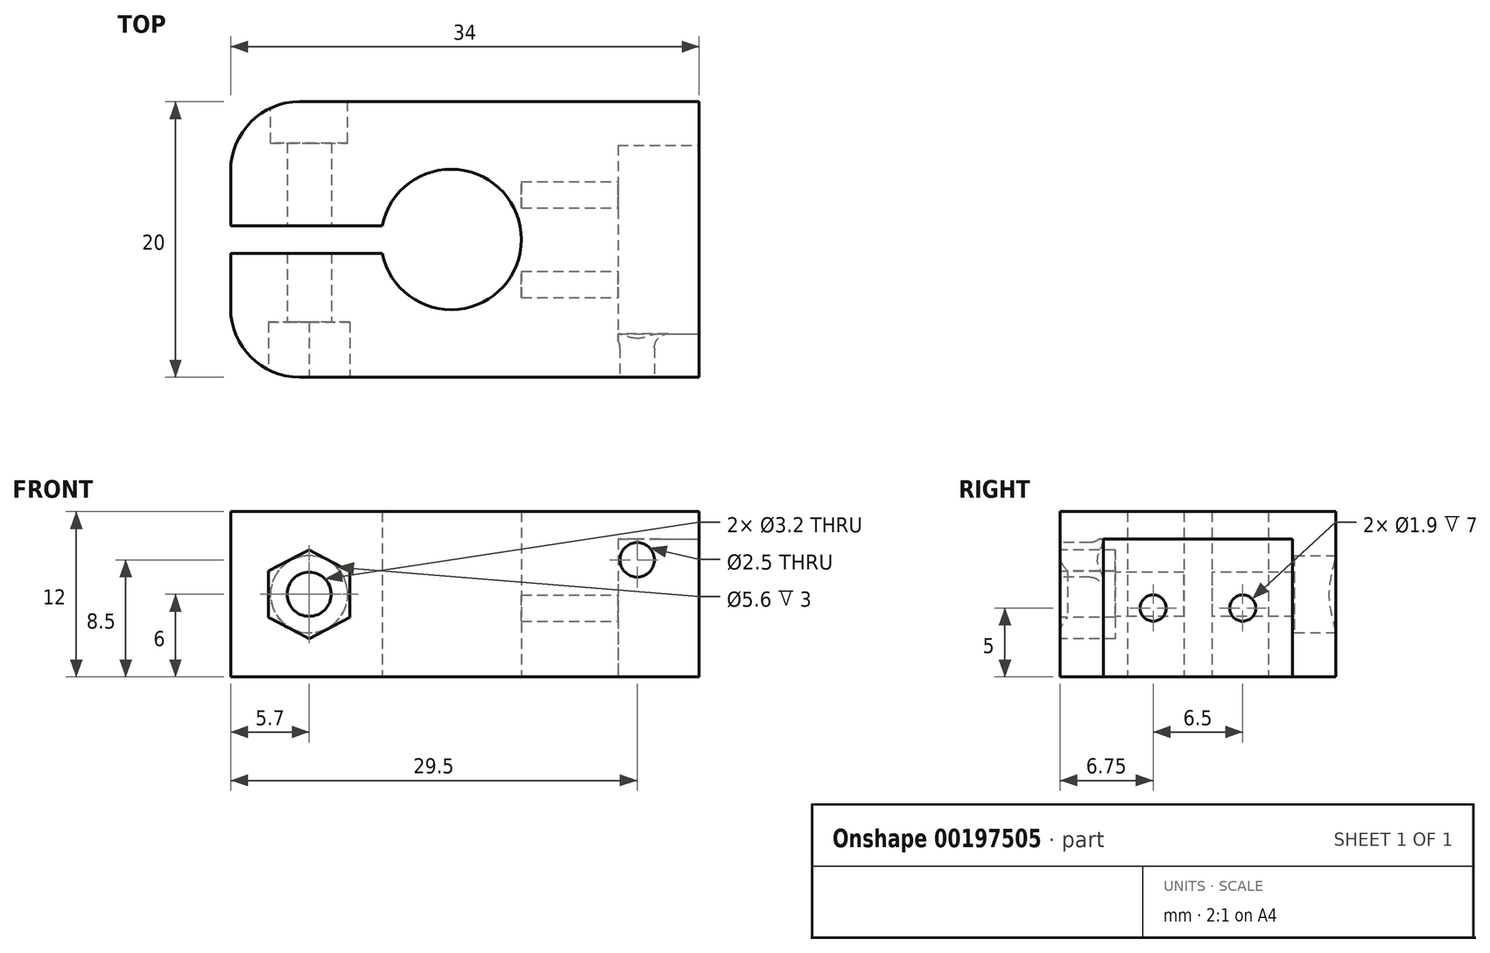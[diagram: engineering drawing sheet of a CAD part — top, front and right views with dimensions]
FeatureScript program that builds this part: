
annotation { "Feature Type Name" : "Feature", "Feature Type Description" : "" }
export const myFeature = defineFeature(function(context is Context, id is Id, definition is map)
    precondition{}
    {
        {
            var Q0;
            Q0=qCreatedBy(makeId("Top.planeOp"),FACE);
            var sketch = newSketch(context, id + "F0", { "sketchPlane" : qUnion([Q0])});
            skLineSegment(sketch, "E0.bottom", {"start": v(-16, 10) * mm, "end": v(18, 10) * mm});
            skLineSegment(sketch, "E0.top", {"start": v(-16, -10) * mm, "end": v(18, -10) * mm});
            skLineSegment(sketch, "E0.left", {"start": v(-16, 10) * mm, "end": v(-16, 1) * mm});
            skLineSegment(sketch, "E0.right", {"start": v(18, 10) * mm, "end": v(18, -10) * mm});
            skArc(sketch, "E1", {"start": v(-5, -1) * mm, "mid": v(5.1, 0) * mm, "end": v(-5, 1) * mm});
            skLineSegment(sketch, "E2.bottom", {"start": v(-16, 0) * mm, "end": v(-4.9, 0) * mm});
            skLineSegment(sketch, "E2.top", {"start": v(-16, 1) * mm, "end": v(-5, 1) * mm});
            skLineSegment(sketch, "E3.MirrorCS", {"start": v(-16, -1) * mm, "end": v(-5, -1) * mm});
            skPoint(sketch, "E4.MirrorCS.end.orphan", {"position": v(-5, -1) * mm});
            skPoint(sketch, "E4.MirrorCS.start.orphan", {"position": v(-4.9, 0) * mm});
            skPoint(sketch, "E5.MirrorCS.end.orphan", {"position": v(-16, -1) * mm});
            skPoint(sketch, "E5.MirrorCS.start.orphan", {"position": v(-16, 0) * mm});
            skLineSegment(sketch, "E6.trimOffspring", {"start": v(-16, -1) * mm, "end": v(-16, -10) * mm});
            skLineSegment(sketch, "E7.bottom", {"start": v(12.1, 6.85) * mm, "end": v(18, 6.85) * mm, "construction": true});
            skLineSegment(sketch, "E7.top", {"start": v(12.1, -6.85) * mm, "end": v(18, -6.85) * mm, "construction": true});
            skLineSegment(sketch, "E7.left", {"start": v(12.1, 6.85) * mm, "end": v(12.1, -6.85) * mm, "construction": true});
            skLineSegment(sketch, "E8.bottom", {"start": v(18, 6.85) * mm, "end": v(18, 6.85) * mm});
            skLineSegment(sketch, "E8.top", {"start": v(14.5, -6.85) * mm, "end": v(18, -6.85) * mm, "construction": true});
            skLineSegment(sketch, "E8.right", {"start": v(18, 6.85) * mm, "end": v(18, -6.85) * mm});
            skLineSegment(sketch, "E9", {"start": v(18, 6.85) * mm, "end": v(18, -6.85) * mm, "construction": true});
            skSolve(sketch);
        }
        {
            var Q0;
            Q0=qSketchRegion(id+"F0",true);
            extrude(context, id + "F1", {"entities" : qUnion([Q0]), "depth" : 12 * mm});
        }
        {
            var Q0;
            Q0=makeQuery(id+"F1.opExtrude","CAP_FACE",FACE,{"disambiguationData":[OSD([sQuery(id+"F0.wireOp",EDGE,"E0.bottom"),sQuery(id+"F0.wireOp",EDGE,"E0.top"),sQuery(id+"F0.wireOp",EDGE,"E0.left"),sQuery(id+"F0.wireOp",EDGE,"E0.right"),sQuery(id+"F0.wireOp",EDGE,"E1"),sQuery(id+"F0.wireOp",EDGE,"E2.top"),sQuery(id+"F0.wireOp",EDGE,"E3.MirrorCS"),sQuery(id+"F0.wireOp",EDGE,"E6.trimOffspring"),sQuery(id+"F0.wireOp",EDGE,"E8.right")])],"isStart":true});
            var sketch = newSketch(context, id + "F2", { "sketchPlane" : qUnion([Q0])});
            skLineSegment(sketch, "E10.0", {"start": v(12.1, -6.85) * mm, "end": v(12.1, 6.85) * mm});
            skLineSegment(sketch, "E11.0", {"start": v(12.1, 6.85) * mm, "end": v(18, 6.85) * mm});
            skLineSegment(sketch, "E12.0", {"start": v(18, 6.85) * mm, "end": v(18, 6.85) * mm});
            skLineSegment(sketch, "E13.0", {"start": v(12.1, -6.85) * mm, "end": v(18, -6.85) * mm});
            skLineSegment(sketch, "E14", {"start": v(18, 6.85) * mm, "end": v(18, -6.85) * mm});
            skSolve(sketch);
        }
        {
            var Q0;
            Q0=qSketchRegion(id+"F2",true);
            extrude(context, id + "F3", {"entities" : qUnion([Q0]), "operationType" : NewBodyOperationType.REMOVE, "oppositeDirection" : true, "depth" : 10 * mm});
        }
        {
            var Q0;
            Q0=makeQuery(id+"F1.opExtrude","SWEPT_FACE",FACE,{"disambiguationData":[OSD([sQuery(id+"F0.wireOp",EDGE,"E0.top")])]});
            var sketch = newSketch(context, id + "F4", { "sketchPlane" : qUnion([Q0])});
            skCircle(sketch, "E15", {"center": v(-10.3, 6) * mm, "radius": 1.6 * mm});
            skPoint(sketch, "E15.centerSnap0", {"position": v(-16, 6) * mm});
            skSolve(sketch);
        }
        {
            var Q0;
            Q0=qSketchRegion(id+"F4",true);
            extrude(context, id + "F5", {"entities" : qUnion([Q0]), "operationType" : NewBodyOperationType.REMOVE, "endBound" : BoundingType.THROUGH_ALL, "oppositeDirection" : true, "depth" : 25 * mm});
        }
        {
            var Q0;
            Q0=makeQuery(id+"F1.opExtrude","SWEPT_FACE",FACE,{"disambiguationData":[OSD([sQuery(id+"F0.wireOp",EDGE,"E0.top")])]});
            var sketch = newSketch(context, id + "F6", { "sketchPlane" : qUnion([Q0])});
            skCircle(sketch, "E16", {"center": v(13.5, 8.5) * mm, "radius": 1.25 * mm});
            skSolve(sketch);
        }
        {
            var Q0;
            Q0=qSketchRegion(id+"F6",true);
            extrude(context, id + "F7", {"entities" : qUnion([Q0]), "operationType" : NewBodyOperationType.REMOVE, "oppositeDirection" : true, "depth" : 16 * mm});
        }
        {
            var Q0;
            Q0=makeQuery(id+"F7.boolean.opBoolean","COPY",EDGE,{"derivedFrom":makeQuery(id+"F7.opExtrude","CAP_EDGE",EDGE,{"disambiguationData":[OSD([sQuery(id+"F6.wireOp",EDGE,"E16")])],"isStart":true})});
            var Q1;
            Q1=makeQuery(id+"F7.boolean.opBoolean","INTERSECT",EDGE,{"derivedFrom":[makeQuery(id+"F3.boolean.opBoolean","COPY",FACE,{"derivedFrom":makeQuery(id+"F3.opExtrude","SWEPT_FACE",FACE,{"disambiguationData":[OSD([sQuery(id+"F2.wireOp",EDGE,"E11.0"),sQuery(id+"F2.wireOp",EDGE,"E12.0")])]})}),makeQuery(id+"F7.opExtrude","SWEPT_FACE",FACE,{"disambiguationData":[OSD([sQuery(id+"F6.wireOp",EDGE,"E16")])]})]});
            fillet(context, id + "F8", {"entities" : qUnion([Q0, Q1]), "radius" : 1 * mm, "tangentPropagation" : true, "allowEdgeOverflow" : false});
        }
        {
            var Q0;
            Q0=makeQuery(id+"F3.boolean.opBoolean","COPY",FACE,{"derivedFrom":makeQuery(id+"F3.opExtrude","SWEPT_FACE",FACE,{"disambiguationData":[OSD([sQuery(id+"F2.wireOp",EDGE,"E10.0")])]})});
            var sketch = newSketch(context, id + "F9", { "sketchPlane" : qUnion([Q0])});
            skCircle(sketch, "E17", {"center": v(46.37, 0.83) * mm, "radius": 0.95 * mm});
            skCircle(sketch, "E18", {"center": v(46.37, -5.67) * mm, "radius": 0.95 * mm});
            skCircle(sketch, "E19", {"center": v(-3.25, 5) * mm, "radius": 0.95 * mm});
            skCircle(sketch, "E20", {"center": v(3.25, 5) * mm, "radius": 0.95 * mm});
            skSolve(sketch);
        }
        {
            var Q0;
            Q0=qSketchRegion(id+"F9",true);
            extrude(context, id + "F10", {"entities" : qUnion([Q0]), "operationType" : NewBodyOperationType.REMOVE, "oppositeDirection" : true, "depth" : 7 * mm});
        }
        {
            var Q0;
            Q0=makeQuery(id+"F1.opExtrude","SWEPT_FACE",FACE,{"disambiguationData":[OSD([sQuery(id+"F0.wireOp",EDGE,"E0.top")])]});
            var sketch = newSketch(context, id + "F11", { "sketchPlane" : qUnion([Q0])});
            skCircle(sketch, "E21.0", {"center": v(-10.3, 6) * mm, "radius": 1.6 * mm});
            skCircle(sketch, "E22", {"center": v(-10.3, 6) * mm, "radius": 2.75 * mm, "construction": true});
            skLineSegment(sketch, "E23", {"start": v(-10.3, 11.28) * mm, "end": v(-10.3, 1.2) * mm, "construction": true});
            skLineSegment(sketch, "E24", {"start": v(-10.3, 6) * mm, "end": v(-14.37, 6) * mm, "construction": true});
            skLineSegment(sketch, "E25", {"start": v(-10.3, 6) * mm, "end": v(-5.72, 6) * mm, "construction": true});
            skLineSegment(sketch, "E26", {"start": v(-7.55, 7.55) * mm, "end": v(-7.55, 4.45) * mm, "construction": true});
            skLineSegment(sketch, "E27", {"start": v(-7.55, 4.45) * mm, "end": v(-10.3, 3) * mm, "construction": true});
            skLineSegment(sketch, "E28", {"start": v(-10.3, 3) * mm, "end": v(-13.05, 4.45) * mm, "construction": true});
            skLineSegment(sketch, "E29", {"start": v(-13.05, 4.45) * mm, "end": v(-13.05, 7.55) * mm, "construction": true});
            skLineSegment(sketch, "E30", {"start": v(-13.05, 7.55) * mm, "end": v(-10.3, 9) * mm, "construction": true});
            skLineSegment(sketch, "E31", {"start": v(-10.3, 9) * mm, "end": v(-7.55, 7.55) * mm, "construction": true});
            skLineSegment(sketch, "E32", {"start": v(-10.31, 9.23) * mm, "end": v(-13.25, 7.69) * mm});
            skLineSegment(sketch, "E33", {"start": v(-13.25, 7.69) * mm, "end": v(-13.25, 4.33) * mm});
            skLineSegment(sketch, "E34", {"start": v(-13.25, 4.33) * mm, "end": v(-10.3, 2.78) * mm});
            skLineSegment(sketch, "E35", {"start": v(-10.3, 2.78) * mm, "end": v(-7.35, 4.33) * mm});
            skLineSegment(sketch, "E36", {"start": v(-7.35, 4.33) * mm, "end": v(-7.35, 7.67) * mm});
            skLineSegment(sketch, "E37", {"start": v(-7.35, 7.67) * mm, "end": v(-10.31, 9.23) * mm});
            skSolve(sketch);
        }
        {
            var Q0;
            Q0=qSketchRegion(id+"F11",true);
            extrude(context, id + "F12", {"entities" : qUnion([Q0]), "operationType" : NewBodyOperationType.REMOVE, "oppositeDirection" : true, "depth" : 4 * mm});
        }
        {
            var Q0;
            Q0=makeQuery(id+"F1.opExtrude","SWEPT_FACE",FACE,{"disambiguationData":[OSD([sQuery(id+"F0.wireOp",EDGE,"E0.bottom")])]});
            var sketch = newSketch(context, id + "F13", { "sketchPlane" : qUnion([Q0])});
            skPoint(sketch, "E38", {"position": v(10.3, 6) * mm});
            skCircle(sketch, "E39", {"center": v(10.3, 6) * mm, "radius": 2.8 * mm});
            skSolve(sketch);
        }
        {
            var Q0;
            Q0=qSketchRegion(id+"F13",true);
            extrude(context, id + "F14", {"entities" : qUnion([Q0]), "operationType" : NewBodyOperationType.REMOVE, "oppositeDirection" : true, "depth" : 3 * mm});
        }
        {
            var Q0;
            Q0=makeQuery(id+"F1.opExtrude","SWEPT_EDGE",EDGE,{"disambiguationData":[OSD([sQuery(id+"F0.wireOp",EDGE,"E0.top"),sQuery(id+"F0.wireOp",EDGE,"E6.trimOffspring")])]});
            var Q1;
            Q1=makeQuery(id+"F1.opExtrude","SWEPT_EDGE",EDGE,{"disambiguationData":[OSD([sQuery(id+"F0.wireOp",EDGE,"E0.bottom"),sQuery(id+"F0.wireOp",EDGE,"E0.left")])]});
            fillet(context, id + "F15", {"entities" : qUnion([Q0, Q1]), "radius" : 5 * mm, "tangentPropagation" : true, "allowEdgeOverflow" : false});
        }
    });
